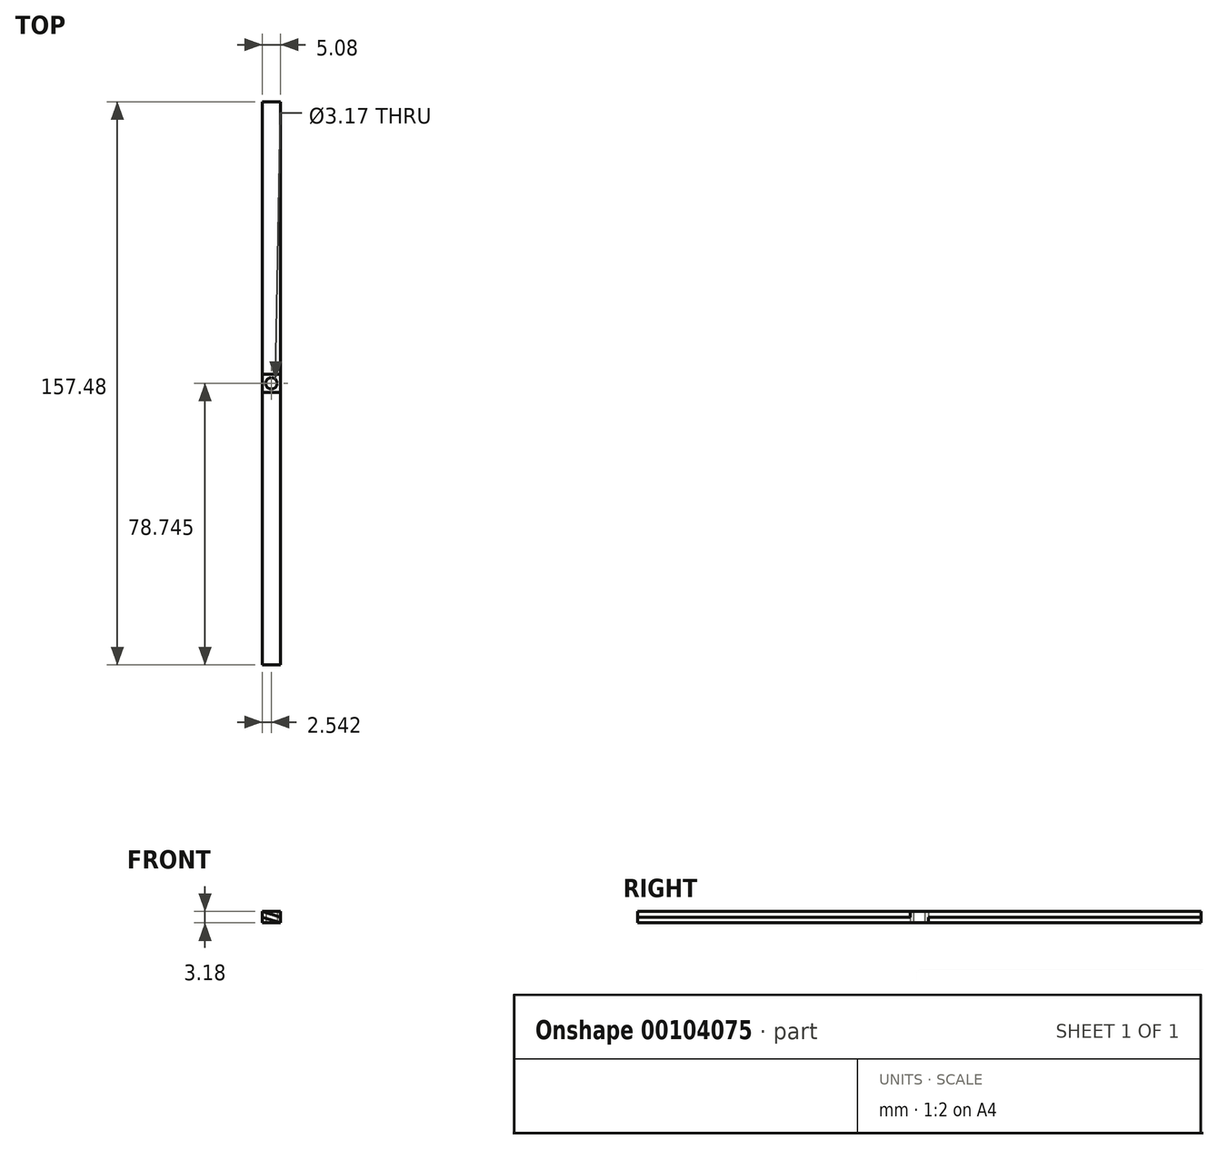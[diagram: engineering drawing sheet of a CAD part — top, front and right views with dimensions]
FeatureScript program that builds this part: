
annotation { "Feature Type Name" : "Feature", "Feature Type Description" : "" }
export const myFeature = defineFeature(function(context is Context, id is Id, definition is map)
    precondition{}
    {
        {
            var Q0;
            Q0=qCreatedBy(makeId("Top.planeOp"),FACE);
            var sketch = newSketch(context, id + "F0", { "sketchPlane" : qUnion([Q0])});
            skLineSegment(sketch, "E0.bottom", {"start": v(-24.54, 15.56) * mm, "end": v(-19.46, 15.56) * mm});
            skLineSegment(sketch, "E0.top", {"start": v(-24.54, 10.48) * mm, "end": v(-19.46, 10.48) * mm});
            skLineSegment(sketch, "E0.left", {"start": v(-24.54, 15.56) * mm, "end": v(-24.54, 10.48) * mm});
            skLineSegment(sketch, "E0.right", {"start": v(-19.46, 15.56) * mm, "end": v(-19.46, 10.48) * mm});
            skCircle(sketch, "E1", {"center": v(-22, 13.02) * mm, "radius": 1.59 * mm});
            skPoint(sketch, "E1.centerSnap0", {"position": v(-22, 15.56) * mm});
            skPoint(sketch, "E1.centerSnap1", {"position": v(-24.54, 13.02) * mm});
            skSolve(sketch);
        }
        {
            var Q0;
            Q0=makeQuery(id+"F0.imprint","IMPRINT",FACE,{"disambiguationData":[TD([[makeQuery(id+"F0.imprint","IMPRINT",EDGE,{"derivedFrom":sQuery(id+"F0.wireOp",EDGE,"E0.bottom")}),-1.0]])]});
            extrude(context, id + "F1", {"entities" : qUnion([Q0]), "depth" : 3.17 * mm});
        }
        {
            var Q0;
            Q0=makeQuery(id+"F1.opExtrude","SWEPT_FACE",FACE,{"disambiguationData":[OSD([sQuery(id+"F0.wireOp",EDGE,"E0.top")])]});
            var sketch = newSketch(context, id + "F2", { "sketchPlane" : qUnion([Q0])});
            skLineSegment(sketch, "E2", {"start": v(-24.54, 1.59) * mm, "end": v(-19.46, 0) * mm});
            skLineSegment(sketch, "E3", {"start": v(-24.54, 3.18) * mm, "end": v(-19.46, 1.59) * mm});
            skSolve(sketch);
        }
        {
            var Q0;
            {var subQ0=sQuery(id+"F2.wireOp",EDGE,"E2");Q0=makeQuery(id+"F2.imprint","IMPRINT",FACE,{"disambiguationData":[TD([[makeQuery(id+"F2.imprint","IMPRINT",EDGE,{"derivedFrom":subQ0}),1.0]])]});}
            extrude(context, id + "F3", {"entities" : qUnion([Q0]), "operationType" : NewBodyOperationType.ADD, "depth" : 76.2 * mm});
        }
        {
            var Q0;
            Q0=makeQuery(id+"F1.opExtrude","SWEPT_FACE",FACE,{"disambiguationData":[OSD([sQuery(id+"F0.wireOp",EDGE,"E0.bottom")])]});
            var sketch = newSketch(context, id + "F4", { "sketchPlane" : qUnion([Q0])});
            skLineSegment(sketch, "E4", {"start": v(19.46, 3.18) * mm, "end": v(24.54, 1.59) * mm});
            skLineSegment(sketch, "E5", {"start": v(19.46, 1.59) * mm, "end": v(24.54, 0) * mm});
            skSolve(sketch);
        }
        {
            var Q0;
            {var subQ0=sQuery(id+"F4.wireOp",EDGE,"E4");Q0=makeQuery(id+"F4.imprint","IMPRINT",FACE,{"disambiguationData":[TD([[makeQuery(id+"F4.imprint","IMPRINT",EDGE,{"derivedFrom":subQ0}),-1.0]])]});}
            extrude(context, id + "F5", {"entities" : qUnion([Q0]), "operationType" : NewBodyOperationType.ADD, "depth" : 76.2 * mm});
        }
    });
